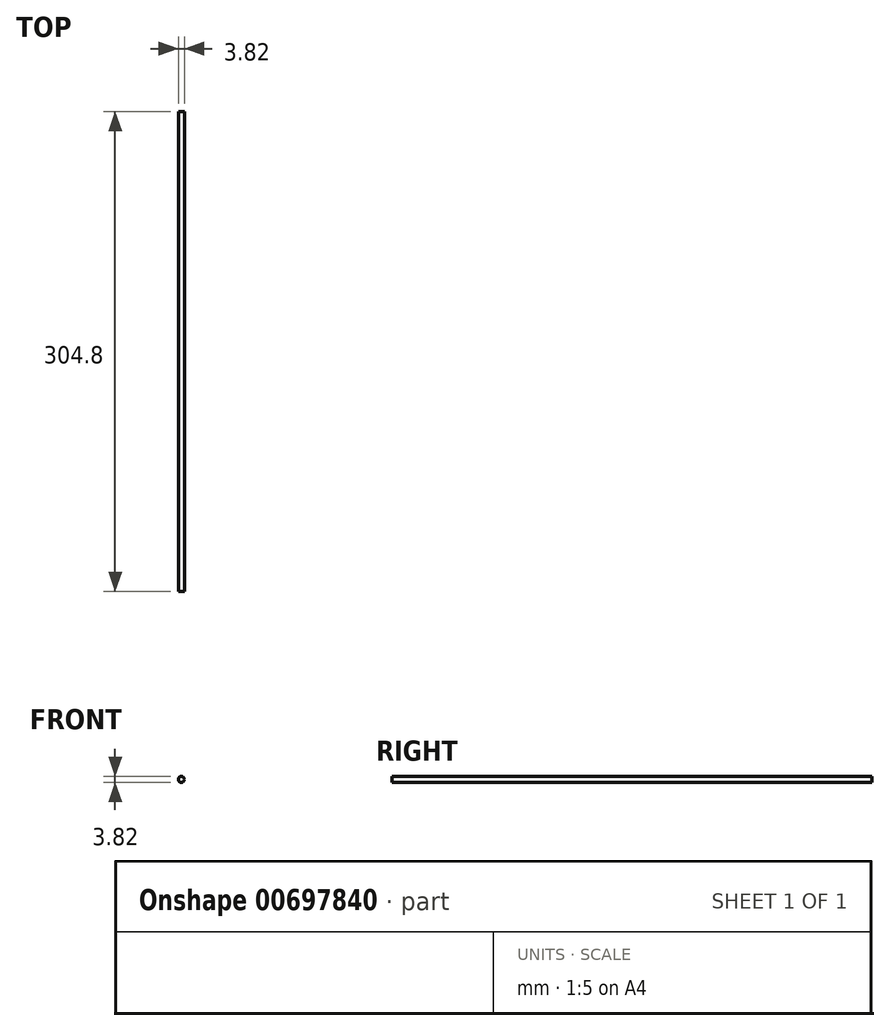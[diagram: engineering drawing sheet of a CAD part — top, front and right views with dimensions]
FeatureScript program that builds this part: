
annotation { "Feature Type Name" : "Feature", "Feature Type Description" : "" }
export const myFeature = defineFeature(function(context is Context, id is Id, definition is map)
    precondition{}
    {
        {
            var Q0;
            Q0=qCreatedBy(makeId("Front.planeOp"),FACE);
            var sketch = newSketch(context, id + "F0", { "sketchPlane" : qUnion([Q0])});
            skCircle(sketch, "E0", {"center": v(0, 0) * mm, "radius": 1.9 * mm});
            skSolve(sketch);
        }
        {
            var Q0;
            Q0 = qSketchRegion(id + "F0", true);
            extrude(context, id + "F1", {"entities" : qUnion([Q0]), "depth" : 304.8 * mm, "offsetDistance" : 25.4 * mm});
        }
    });
